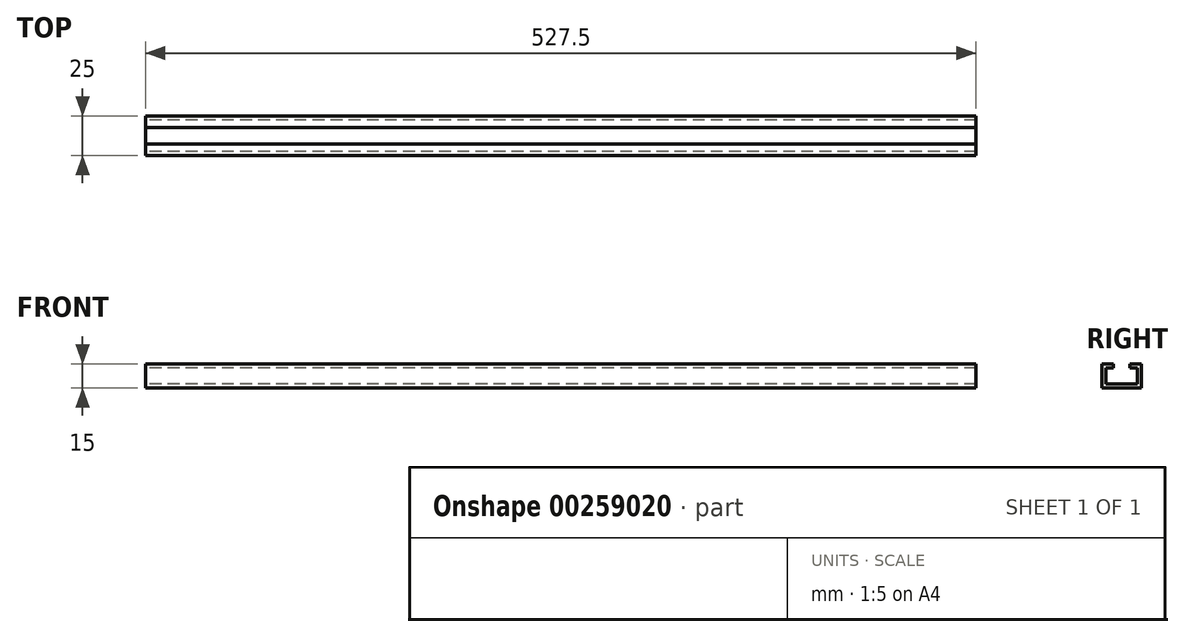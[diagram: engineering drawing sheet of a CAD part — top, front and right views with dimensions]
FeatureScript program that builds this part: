
annotation { "Feature Type Name" : "Feature", "Feature Type Description" : "" }
export const myFeature = defineFeature(function(context is Context, id is Id, definition is map)
    precondition{}
    {
        {
            var Q0;
            Q0=qCreatedBy(makeId("Right.planeOp"),FACE);
            var sketch = newSketch(context, id + "F0", { "sketchPlane" : qUnion([Q0])});
            skLineSegment(sketch, "E0.bottom", {"start": v(-12.5, 15) * mm, "end": v(-10, 15) * mm});
            skLineSegment(sketch, "E0.top", {"start": v(-12.5, 0) * mm, "end": v(12.5, 0) * mm});
            skLineSegment(sketch, "E0.left", {"start": v(-12.5, 15) * mm, "end": v(-12.5, 0) * mm});
            skLineSegment(sketch, "E0.right", {"start": v(12.5, 15) * mm, "end": v(12.5, 0) * mm});
            skLineSegment(sketch, "E1.0", {"start": v(-10, 12.5) * mm, "end": v(-10, 2.5) * mm});
            skLineSegment(sketch, "E2.0", {"start": v(-10, 2.5) * mm, "end": v(10, 2.5) * mm});
            skLineSegment(sketch, "E3.0", {"start": v(10, 12.5) * mm, "end": v(10, 2.5) * mm});
            skLineSegment(sketch, "E4.trimOffspring", {"start": v(10, 15) * mm, "end": v(12.5, 15) * mm});
            skLineSegment(sketch, "E5.bottom", {"start": v(-12.5, 15) * mm, "end": v(-5.2, 15) * mm});
            skLineSegment(sketch, "E5.top", {"start": v(-10, 12.5) * mm, "end": v(-5.2, 12.5) * mm});
            skLineSegment(sketch, "E5.left", {"start": v(-12.5, 15) * mm, "end": v(-12.5, 12.5) * mm});
            skLineSegment(sketch, "E5.right", {"start": v(12.5, 15) * mm, "end": v(12.5, 12.5) * mm});
            skLineSegment(sketch, "E6", {"start": v(-5.2, 15) * mm, "end": v(-5.2, 12.5) * mm});
            skLineSegment(sketch, "E7", {"start": v(5.2, 15) * mm, "end": v(5.2, 12.5) * mm});
            skLineSegment(sketch, "E8.trimOffspring", {"start": v(5.2, 12.5) * mm, "end": v(10, 12.5) * mm});
            skLineSegment(sketch, "E9.trimOffspring", {"start": v(5.2, 15) * mm, "end": v(12.5, 15) * mm});
            skSolve(sketch);
        }
        {
            var Q0;
            Q0=makeQuery(id+"F0.imprint","IMPRINT",FACE,{"disambiguationData":[TD([[makeQuery(id+"F0.imprint","IMPRINT",EDGE,{"derivedFrom":sQuery(id+"F0.wireOp",EDGE,"E0.bottom")}),-1.0]])]});
            var Q1;
            Q1=makeQuery(id+"F0.imprint","IMPRINT",FACE,{"disambiguationData":[TD([[makeQuery(id+"F0.imprint","IMPRINT",EDGE,{"derivedFrom":sQuery(id+"F0.wireOp",EDGE,"E0.top")}),1.0]])]});
            extrude(context, id + "F1", {"entities" : qUnion([Q0, Q1]), "depth" : (580 - 20 - 12.5 - 20) * mm, "offsetDistance" : 25 * mm, "symmetric" : true});
        }
    });
